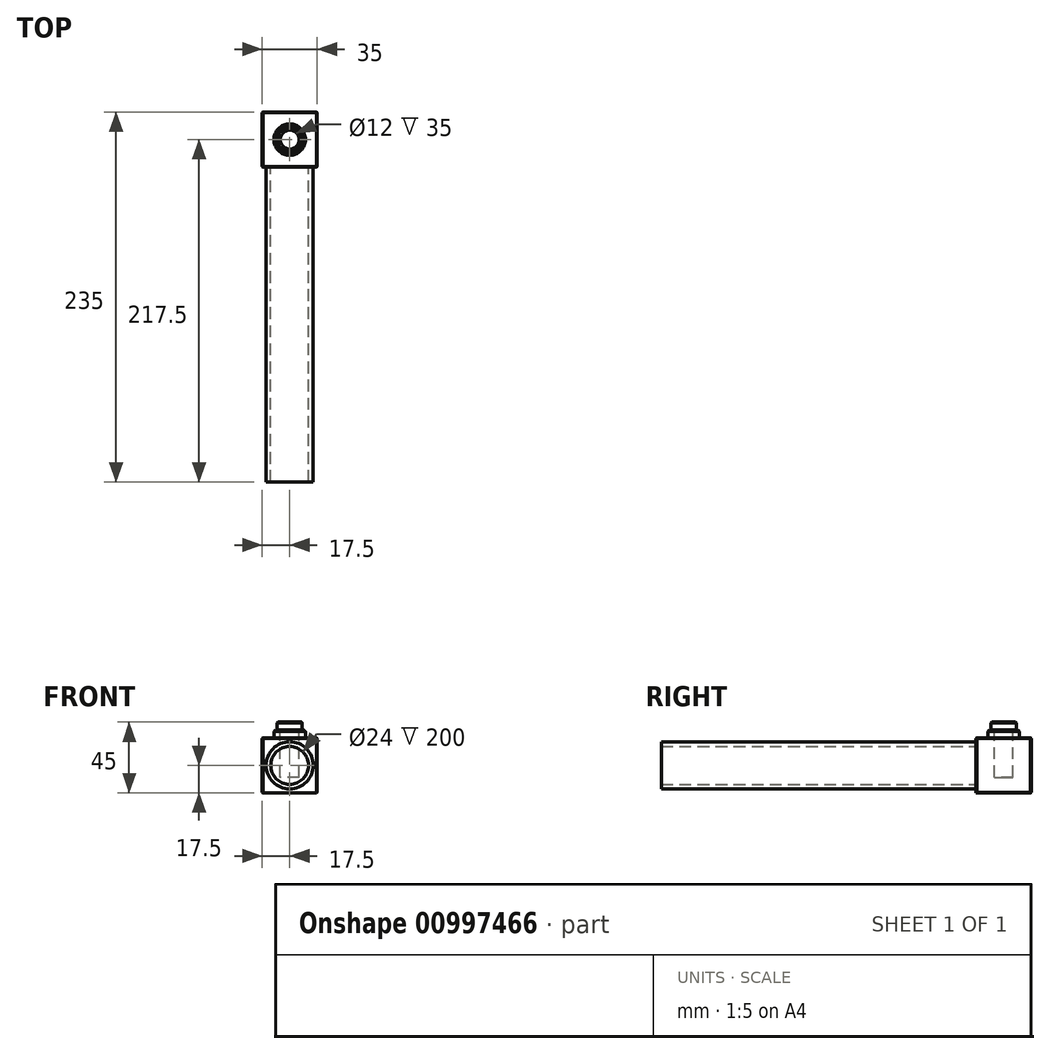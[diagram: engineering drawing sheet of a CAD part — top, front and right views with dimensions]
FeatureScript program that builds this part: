
annotation { "Feature Type Name" : "Feature", "Feature Type Description" : "" }
export const myFeature = defineFeature(function(context is Context, id is Id, definition is map)
    precondition{}
    {
        {
            var Q0;
            Q0=qCreatedBy(makeId("Front.planeOp"),FACE);
            var sketch = newSketch(context, id + "F0", { "sketchPlane" : qUnion([Q0])});
            skLineSegment(sketch, "E0.bottom", {"start": v(-17.5, 17.5) * mm, "end": v(17.5, 17.5) * mm});
            skLineSegment(sketch, "E0.top", {"start": v(-17.5, -17.5) * mm, "end": v(17.5, -17.5) * mm});
            skLineSegment(sketch, "E0.left", {"start": v(-17.5, 17.5) * mm, "end": v(-17.5, -17.5) * mm});
            skLineSegment(sketch, "E0.right", {"start": v(17.5, 17.5) * mm, "end": v(17.5, -17.5) * mm});
            skSolve(sketch);
        }
        {
            var Q0;
            Q0=makeQuery(id+"F0.imprint","IMPRINT",FACE,{"disambiguationData":[TD([[makeQuery(id+"F0.imprint","IMPRINT",EDGE,{"derivedFrom":sQuery(id+"F0.wireOp",EDGE,"E0.bottom")}),-1.0]])]});
            var Q1;
            Q1 = qSketchRegion(id + "F2", true);
            extrude(context, id + "F1", {"entities" : qUnion([Q0, Q1]), "depth" : 35 * mm, "offsetDistance" : 25 * mm});
        }
        {
            var Q0;
            Q0=makeQuery(id+"F1.opExtrude","CAP_FACE",FACE,{"disambiguationData":[OSD([sQuery(id+"F0.wireOp",EDGE,"E0.bottom"),sQuery(id+"F0.wireOp",EDGE,"E0.top"),sQuery(id+"F0.wireOp",EDGE,"E0.left"),sQuery(id+"F0.wireOp",EDGE,"E0.right")])],"isStart":false});
            var sketch = newSketch(context, id + "F2", { "sketchPlane" : qUnion([Q0])});
            skCircle(sketch, "E1", {"center": v(0, 0) * mm, "radius": 15 * mm});
            skCircle(sketch, "E2", {"center": v(0, 0) * mm, "radius": 12 * mm});
            skSolve(sketch);
        }
        {
            var Q0;
            Q0=makeQuery(id+"F2.imprint","IMPRINT",FACE,{"disambiguationData":[TD([[makeQuery(id+"F2.imprint","IMPRINT",EDGE,{"derivedFrom":sQuery(id+"F2.wireOp",EDGE,"E1")}),1.0]])]});
            extrude(context, id + "F3", {"entities" : qUnion([Q0]), "operationType" : NewBodyOperationType.ADD, "depth" : 200 * mm, "offsetDistance" : 25 * mm});
        }
        {
            var Q0;
            Q0=makeQuery(id+"F1.opExtrude","SWEPT_FACE",FACE,{"disambiguationData":[OSD([sQuery(id+"F0.wireOp",EDGE,"E0.bottom")])]});
            var sketch = newSketch(context, id + "F4", { "sketchPlane" : qUnion([Q0])});
            skCircle(sketch, "E3", {"center": v(0, -17.5) * mm, "radius": 10 * mm});
            skSolve(sketch);
        }
        {
            var Q0;
            Q0=makeQuery(id+"F4.imprint","IMPRINT",FACE,{"disambiguationData":[TD([[makeQuery(id+"F4.imprint","IMPRINT",EDGE,{"derivedFrom":sQuery(id+"F4.wireOp",EDGE,"E3")}),1.0]])]});
            extrude(context, id + "F5", {"entities" : qUnion([Q0]), "operationType" : NewBodyOperationType.ADD, "depth" : 5 * mm, "offsetDistance" : 25 * mm});
        }
        {
            var Q0;
            Q0=makeQuery(id+"F5.opExtrude","CAP_FACE",FACE,{"disambiguationData":[OSD([sQuery(id+"F4.wireOp",EDGE,"E3")])],"isStart":false});
            var sketch = newSketch(context, id + "F6", { "sketchPlane" : qUnion([Q0])});
            skCircle(sketch, "E4", {"center": v(0, -17.5) * mm, "radius": 8 * mm});
            skSolve(sketch);
        }
        {
            var Q0;
            Q0=makeQuery(id+"F6.imprint","IMPRINT",FACE,{"disambiguationData":[TD([[makeQuery(id+"F6.imprint","IMPRINT",EDGE,{"derivedFrom":sQuery(id+"F6.wireOp",EDGE,"E4")}),1.0]])]});
            extrude(context, id + "F7", {"entities" : qUnion([Q0]), "operationType" : NewBodyOperationType.ADD, "depth" : 5 * mm, "offsetDistance" : 25 * mm});
        }
        {
            var Q0;
            Q0=makeQuery(id+"F5.opExtrude","CAP_EDGE",EDGE,{"disambiguationData":[OSD([sQuery(id+"F4.wireOp",EDGE,"E3")])],"isStart":false});
            chamfer(context, id + "F8", {"entities" : qUnion([Q0]), "width" : 1 * mm, "tangentPropagation" : true});
        }
        {
            var Q0;
            Q0=makeQuery(id+"F7.opExtrude","CAP_EDGE",EDGE,{"disambiguationData":[OSD([sQuery(id+"F6.wireOp",EDGE,"E4")])],"isStart":false});
            chamfer(context, id + "F9", {"entities" : qUnion([Q0]), "width" : 0.5 * mm, "tangentPropagation" : true});
        }
        {
            var Q0;
            Q0=makeQuery(id+"F7.opExtrude","CAP_FACE",FACE,{"disambiguationData":[OSD([sQuery(id+"F6.wireOp",EDGE,"E4")])],"isStart":false});
            var sketch = newSketch(context, id + "F10", { "sketchPlane" : qUnion([Q0])});
            skCircle(sketch, "E5", {"center": v(0, -17.5) * mm, "radius": 6 * mm});
            skSolve(sketch);
        }
        {
            var Q0;
            Q0=makeQuery(id+"F10.imprint","IMPRINT",FACE,{"disambiguationData":[TD([[makeQuery(id+"F10.imprint","IMPRINT",EDGE,{"derivedFrom":sQuery(id+"F10.wireOp",EDGE,"E5")}),1.0]])]});
            extrude(context, id + "F11", {"entities" : qUnion([Q0]), "operationType" : NewBodyOperationType.REMOVE, "oppositeDirection" : true, "depth" : 35 * mm, "offsetDistance" : 25 * mm});
        }
        {
            var Q0;
            Q0=makeQuery(id+"F1.opExtrude","CAP_EDGE",EDGE,{"disambiguationData":[OSD([sQuery(id+"F0.wireOp",EDGE,"E0.bottom")])],"isStart":false});
            var Q1;
            Q1=makeQuery(id+"F1.opExtrude","SWEPT_EDGE",EDGE,{"disambiguationData":[OSD([sQuery(id+"F0.wireOp",EDGE,"E0.bottom"),sQuery(id+"F0.wireOp",EDGE,"E0.left")])]});
            var Q2;
            Q2=makeQuery(id+"F1.opExtrude","SWEPT_EDGE",EDGE,{"disambiguationData":[OSD([sQuery(id+"F0.wireOp",EDGE,"E0.bottom"),sQuery(id+"F0.wireOp",EDGE,"E0.right")])]});
            var Q3;
            Q3=makeQuery(id+"F1.opExtrude","CAP_EDGE",EDGE,{"disambiguationData":[OSD([sQuery(id+"F0.wireOp",EDGE,"E0.bottom")])],"isStart":true});
            var Q4;
            Q4=makeQuery(id+"F1.opExtrude","CAP_EDGE",EDGE,{"disambiguationData":[OSD([sQuery(id+"F0.wireOp",EDGE,"E0.right")])],"isStart":true});
            var Q5;
            Q5=makeQuery(id+"F1.opExtrude","CAP_EDGE",EDGE,{"disambiguationData":[OSD([sQuery(id+"F0.wireOp",EDGE,"E0.right")])],"isStart":false});
            var Q6;
            Q6=makeQuery(id+"F1.opExtrude","SWEPT_EDGE",EDGE,{"disambiguationData":[OSD([sQuery(id+"F0.wireOp",EDGE,"E0.top"),sQuery(id+"F0.wireOp",EDGE,"E0.right")])]});
            var Q7;
            Q7=makeQuery(id+"F1.opExtrude","CAP_EDGE",EDGE,{"disambiguationData":[OSD([sQuery(id+"F0.wireOp",EDGE,"E0.top")])],"isStart":true});
            var Q8;
            Q8=makeQuery(id+"F1.opExtrude","CAP_EDGE",EDGE,{"disambiguationData":[OSD([sQuery(id+"F0.wireOp",EDGE,"E0.left")])],"isStart":false});
            var Q9;
            Q9=makeQuery(id+"F1.opExtrude","SWEPT_EDGE",EDGE,{"disambiguationData":[OSD([sQuery(id+"F0.wireOp",EDGE,"E0.top"),sQuery(id+"F0.wireOp",EDGE,"E0.left")])]});
            var Q10;
            Q10=makeQuery(id+"F1.opExtrude","CAP_EDGE",EDGE,{"disambiguationData":[OSD([sQuery(id+"F0.wireOp",EDGE,"E0.left")])],"isStart":true});
            chamfer(context, id + "F12", {"entities" : qUnion([Q0, Q1, Q2, Q3, Q4, Q5, Q6, Q7, Q8, Q9, Q10]), "width" : 0.5 * mm, "tangentPropagation" : true});
        }
    });
